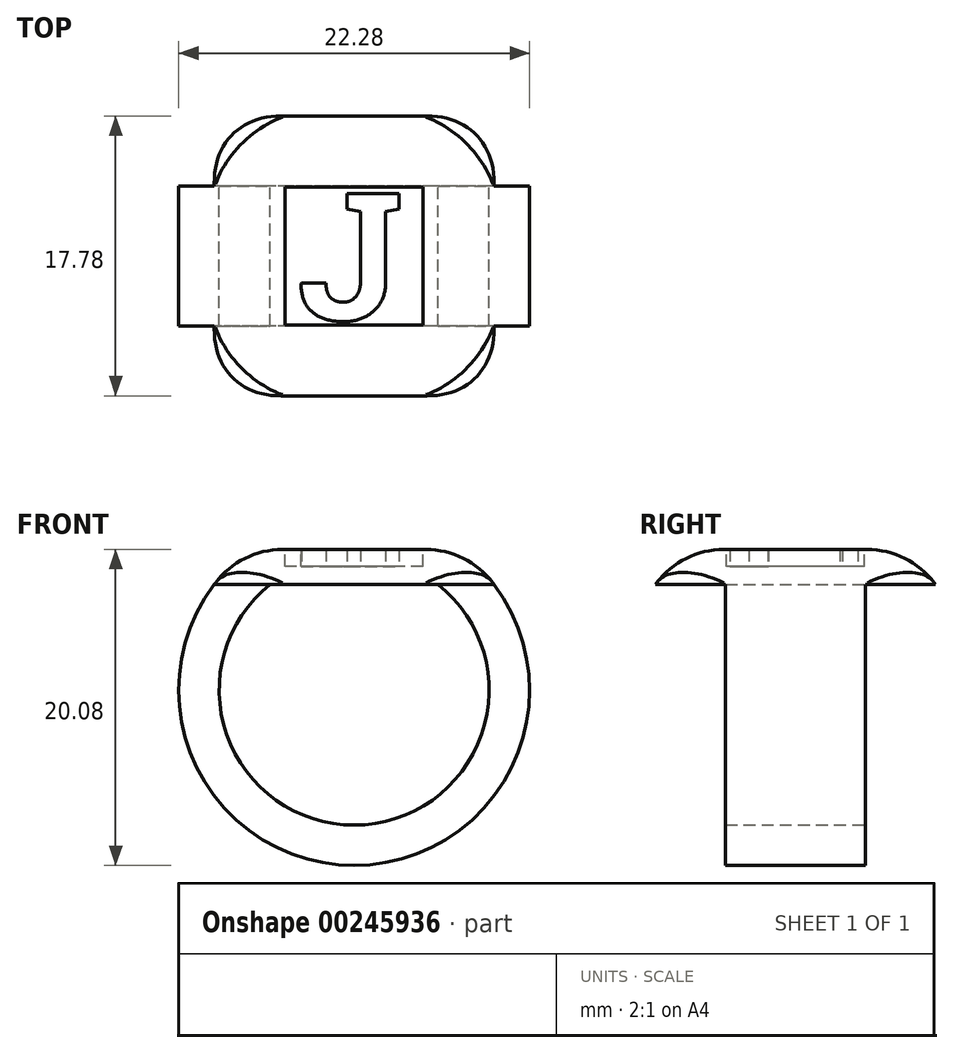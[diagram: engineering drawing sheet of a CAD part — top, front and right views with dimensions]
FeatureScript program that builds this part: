
annotation { "Feature Type Name" : "Feature", "Feature Type Description" : "" }
export const myFeature = defineFeature(function(context is Context, id is Id, definition is map)
    precondition{}
    {
        {
            var Q0;
            Q0=qCreatedBy(makeId("Top.planeOp"),FACE);
            var sketch = newSketch(context, id + "F0", { "sketchPlane" : qUnion([Q0])});
            skLineSegment(sketch, "E0.bottom", {"start": v(-12.7, 12.7) * mm, "end": v(12.7, 12.7) * mm});
            skLineSegment(sketch, "E0.top", {"start": v(-12.7, -12.7) * mm, "end": v(12.7, -12.7) * mm});
            skLineSegment(sketch, "E0.left", {"start": v(-12.7, 12.7) * mm, "end": v(-12.7, -12.7) * mm});
            skLineSegment(sketch, "E0.right", {"start": v(12.7, 12.7) * mm, "end": v(12.7, -12.7) * mm});
            skPoint(sketch, "E0.middle", {"position": v(0, 0) * mm});
            skSolve(sketch);
        }
        {
            var Q0;
            Q0=makeQuery(id+"F0.imprint","IMPRINT",FACE,{"disambiguationData":[TD([[makeQuery(id+"F0.imprint","IMPRINT",EDGE,{"derivedFrom":sQuery(id+"F0.wireOp",EDGE,"E0.bottom")}),-1.0]])]});
            extrude(context, id + "F1", {"entities" : qUnion([Q0]), "depth" : 3.17 * mm, "hasDraft" : true, "draftAngle" : 37 * degree, "draftPullDirection" : true});
        }
        {
            var Q0;
            Q0=qCreatedBy(makeId("Front.planeOp"),FACE);
            var sketch = newSketch(context, id + "F2", { "sketchPlane" : qUnion([Q0])});
            skArc(sketch, "E1", {"start": v(-10.16, 0) * mm, "mid": v(0, -23.56) * mm, "end": v(10.16, 0) * mm});
            skSolve(sketch);
        }
        {
            var Q0;
            Q0=makeQuery(id+"F1.opExtrude","CAP_FACE",FACE,{"disambiguationData":[OSD([sQuery(id+"F0.wireOp",EDGE,"E0.bottom"),sQuery(id+"F0.wireOp",EDGE,"E0.top"),sQuery(id+"F0.wireOp",EDGE,"E0.left"),sQuery(id+"F0.wireOp",EDGE,"E0.right")])],"isStart":true});
            var sketch = newSketch(context, id + "F3", { "sketchPlane" : qUnion([Q0])});
            skLineSegment(sketch, "E2.bottom", {"start": v(12.7, 6.35) * mm, "end": v(7.62, 6.35) * mm});
            skLineSegment(sketch, "E2.top", {"start": v(12.7, -6.35) * mm, "end": v(7.62, -6.35) * mm});
            skLineSegment(sketch, "E2.left", {"start": v(12.7, 6.35) * mm, "end": v(12.7, -6.35) * mm});
            skLineSegment(sketch, "E2.right", {"start": v(7.62, 6.35) * mm, "end": v(7.62, -6.35) * mm});
            skPoint(sketch, "E2.middle", {"position": v(10.16, 0) * mm});
            skSolve(sketch);
        }
        {
            var Q0;
            Q0 = qSketchRegion(id + "F3", true);
            var Q1;
            Q1 = qConstructionFilter(qBodyType(qCreatedBy(id + "F2" ,EDGE), BodyType.WIRE), ConstructionObject.NO);
            sweep(context, id + "F4", {"operationType" : NewBodyOperationType.ADD, "profiles" : qUnion([Q0]), "path" : qUnion([Q1])});
        }
        {
            var Q0;
            Q0=qCreatedBy(makeId("Front.planeOp"),FACE);
            var sketch = newSketch(context, id + "F5", { "sketchPlane" : qUnion([Q0])});
            skArc(sketch, "E3", {"start": v(-7.62, 0) * mm, "mid": v(-8.9, -1.18) * mm, "end": v(-10.01, -2.54) * mm});
            skLineSegment(sketch, "E4.0", {"start": v(-10.16, 0) * mm, "end": v(-7.62, 0) * mm});
            skLineSegment(sketch, "E5.0", {"start": v(-10.16, 0) * mm, "end": v(-10.01, -2.54) * mm});
            skSolve(sketch);
        }
        {
            var Q0;
            Q0 = qSketchRegion(id + "F5", true);
            var Q1;
            Q1 = qConstructionFilter(qBodyType(qCreatedBy(id + "F5" ,EDGE), BodyType.WIRE), ConstructionObject.NO);
            extrude(context, id + "F6", {"entities" : qUnion([Q0]), "operationType" : NewBodyOperationType.ADD, "surfaceEntities" : qUnion([Q1]), "endBound" : BoundingType.SYMMETRIC, "depth" : 12.7 * mm});
        }
        {
            var Q0;
            Q0=makeQuery(id+"F1.opExtrude","SWEPT_EDGE",EDGE,{"disambiguationData":[OSD([sQuery(id+"F0.wireOp",EDGE,"E0.top"),sQuery(id+"F0.wireOp",EDGE,"E0.right")])]});
            var Q1;
            Q1=makeQuery(id+"F1.opExtrude","SWEPT_EDGE",EDGE,{"disambiguationData":[OSD([sQuery(id+"F0.wireOp",EDGE,"E0.top"),sQuery(id+"F0.wireOp",EDGE,"E0.left")])]});
            var Q2;
            Q2=makeQuery(id+"F1.opExtrude","SWEPT_EDGE",EDGE,{"disambiguationData":[OSD([sQuery(id+"F0.wireOp",EDGE,"E0.bottom"),sQuery(id+"F0.wireOp",EDGE,"E0.left")])]});
            var Q3;
            Q3=makeQuery(id+"F1.opExtrude","SWEPT_EDGE",EDGE,{"disambiguationData":[OSD([sQuery(id+"F0.wireOp",EDGE,"E0.bottom"),sQuery(id+"F0.wireOp",EDGE,"E0.right")])]});
            fillet(context, id + "F7", {"entities" : qUnion([Q0, Q1, Q2, Q3]), "radius" : 7.62 * mm, "tangentPropagation" : true, "allowEdgeOverflow" : false});
        }
        {
            var Q0;
            Q0=makeQuery(id+"F1.opExtrude","CAP_EDGE",EDGE,{"disambiguationData":[OSD([sQuery(id+"F0.wireOp",EDGE,"E0.bottom")])],"isStart":false});
            fillet(context, id + "F8", {"entities" : qUnion([Q0]), "radius" : 7.62 * mm, "tangentPropagation" : true, "allowEdgeOverflow" : false});
        }
        {
            var Q0;
            Q0=makeQuery(id+"F1.opExtrude","CAP_FACE",FACE,{"disambiguationData":[OSD([sQuery(id+"F0.wireOp",EDGE,"E0.bottom"),sQuery(id+"F0.wireOp",EDGE,"E0.top"),sQuery(id+"F0.wireOp",EDGE,"E0.left"),sQuery(id+"F0.wireOp",EDGE,"E0.right")])],"isStart":false});
            var sketch = newSketch(context, id + "F9", { "sketchPlane" : qUnion([Q0])});
            skLineSegment(sketch, "E6.0", {"start": v(-6.25, 6.25) * mm, "end": v(-6.25, -6.25) * mm});
            skLineSegment(sketch, "E6.1", {"start": v(6.25, 6.25) * mm, "end": v(-6.25, 6.25) * mm});
            skLineSegment(sketch, "E6.2", {"start": v(6.25, -6.25) * mm, "end": v(6.25, 6.25) * mm});
            skLineSegment(sketch, "E6.3", {"start": v(-6.25, -6.25) * mm, "end": v(6.25, -6.25) * mm});
            skSolve(sketch);
        }
        {
            var Q0;
            Q0=makeQuery(id+"F9.imprint","IMPRINT",FACE,{"disambiguationData":[TD([[makeQuery(id+"F9.imprint","IMPRINT",EDGE,{"derivedFrom":sQuery(id+"F9.wireOp",EDGE,"E6.0")}),1.0]])]});
            extrude(context, id + "F10", {"entities" : qUnion([Q0]), "operationType" : NewBodyOperationType.REMOVE, "oppositeDirection" : true, "depth" : 1.52 * mm});
        }
        {
            var Q0;
            Q0=makeQuery(id+"F10.boolean.opBoolean","COPY",FACE,{"derivedFrom":makeQuery(id+"F10.opExtrude","CAP_FACE",FACE,{"disambiguationData":[OSD([sQuery(id+"F9.wireOp",EDGE,"E6.0"),sQuery(id+"F9.wireOp",EDGE,"E6.1"),sQuery(id+"F9.wireOp",EDGE,"E6.2"),sQuery(id+"F9.wireOp",EDGE,"E6.3")])],"isStart":false})});
            var sketch = newSketch(context, id + "F11", { "sketchPlane" : qUnion([Q0])});
            skText(sketch, "E7", { "text": "J", "fontName": "RobotoSlab-Bold.ttf"});
            const initialGuessF11  = {"E7": [-0.00508, -0.0058, 1, 0, 0.0116]};
            skSetInitialGuess(sketch, initialGuessF11);
            skSolve(sketch);
        }
        {
            var Q0;
            Q0=makeQuery(id+"F11.imprint","IMPRINT",FACE,{"disambiguationData":[TD([[makeQuery(id+"F11.imprint","IMPRINT",EDGE,{"derivedFrom":sQuery(id+"F11.wireOp",EDGE,"E7.sketch_text.stroke-0")}),-1.0]])]});
            extrude(context, id + "F12", {"entities" : qUnion([Q0]), "operationType" : NewBodyOperationType.ADD, "depth" : 1.52 * mm});
        }
        {
            var Q0;
            Q0=makeQuery(id+"F1.opExtrude","SWEPT_BODY",BODY,{"disambiguationData":[OSD([sQuery(id+"F0.wireOp",EDGE,"E0.bottom"),sQuery(id+"F0.wireOp",EDGE,"E0.top"),sQuery(id+"F0.wireOp",EDGE,"E0.left"),sQuery(id+"F0.wireOp",EDGE,"E0.right")])]});
            var Q1;
            Q1=sQuery(id+"F2.wireOp",VERTEX,"E1.center");
            transform(context, id + "F13", {"entities" : qUnion([Q0]), "transformType" : TransformType.SCALE_UNIFORMLY, "scale" : .7, "scalePoint" : qUnion([Q1]), "makeCopy" : false});
        }
    });
